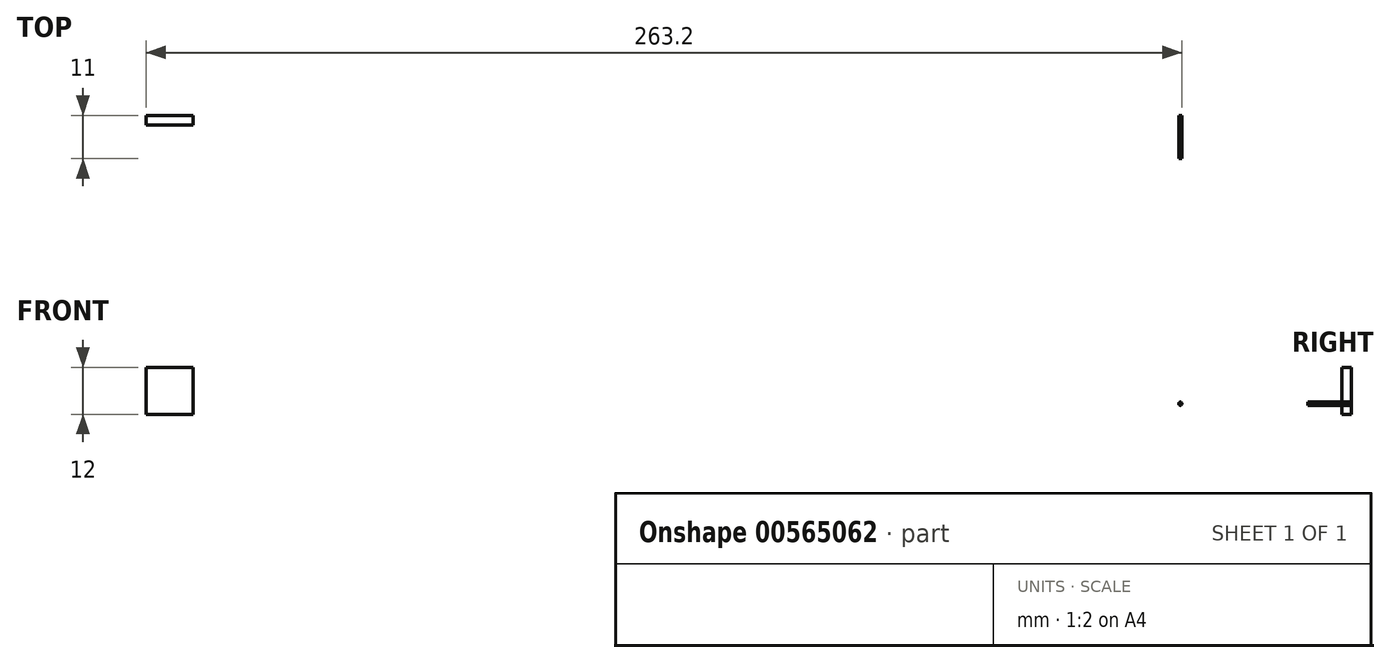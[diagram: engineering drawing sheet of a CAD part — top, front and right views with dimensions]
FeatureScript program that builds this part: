
annotation { "Feature Type Name" : "Feature", "Feature Type Description" : "" }
export const myFeature = defineFeature(function(context is Context, id is Id, definition is map)
    precondition{}
    {
        {
            var Q0;
            Q0=qCreatedBy(makeId("Front.planeOp"),FACE);
            var sketch = newSketch(context, id + "F0", { "sketchPlane" : qUnion([Q0])});
            skCircle(sketch, "E0", {"center": v(24.16, 27.6) * mm, "radius": 0.4 * mm});
            skSolve(sketch);
        }
        {
            var Q0;
            Q0=makeQuery(id+"F0.imprint","IMPRINT",FACE,{"disambiguationData":[TD([[makeQuery(id+"F0.imprint","IMPRINT",EDGE,{"derivedFrom":sQuery(id+"F0.wireOp",EDGE,"E0")}),1.0]])]});
            extrude(context, id + "F1", {"entities" : qUnion([Q0]), "depth" : 11 * mm, "offsetDistance" : 25 * mm});
        }
        {
            var Q0;
            Q0=qCreatedBy(makeId("Front.planeOp"),FACE);
            var sketch = newSketch(context, id + "F2", { "sketchPlane" : qUnion([Q0])});
            skLineSegment(sketch, "E1.bottom", {"start": v(-226.63, 36.85) * mm, "end": v(-238.63, 36.85) * mm});
            skLineSegment(sketch, "E1.top", {"start": v(-226.63, 24.85) * mm, "end": v(-238.63, 24.85) * mm});
            skLineSegment(sketch, "E1.left", {"start": v(-226.63, 36.85) * mm, "end": v(-226.63, 24.85) * mm});
            skLineSegment(sketch, "E1.right", {"start": v(-238.63, 36.85) * mm, "end": v(-238.63, 24.85) * mm});
            skSolve(sketch);
        }
        {
            var Q0;
            Q0=makeQuery(id+"F2.imprint","IMPRINT",FACE,{"disambiguationData":[TD([[makeQuery(id+"F2.imprint","IMPRINT",EDGE,{"derivedFrom":sQuery(id+"F2.wireOp",EDGE,"E1.bottom")}),1.0]])]});
            extrude(context, id + "F3", {"entities" : qUnion([Q0]), "depth" : 2.4 * mm, "offsetDistance" : 25 * mm});
        }
    });
